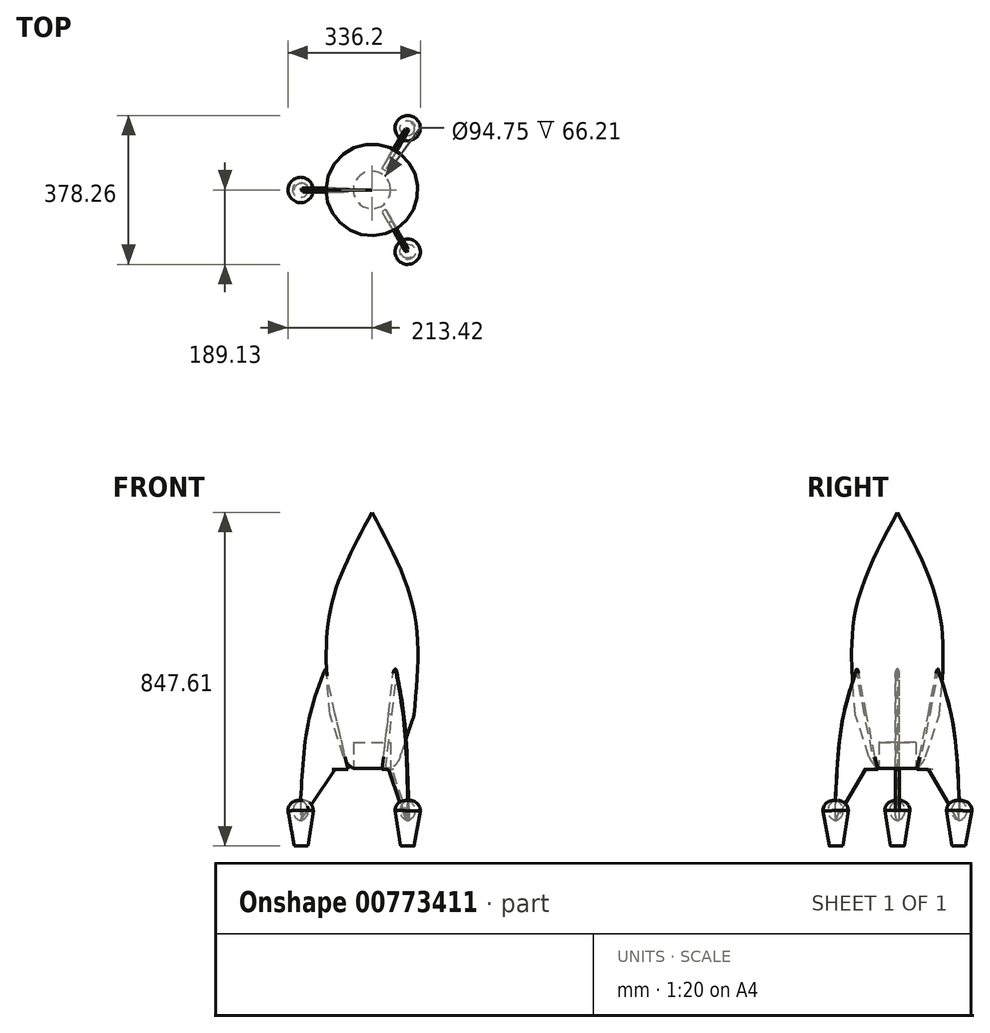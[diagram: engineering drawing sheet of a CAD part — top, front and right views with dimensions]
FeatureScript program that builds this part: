
annotation { "Feature Type Name" : "Feature", "Feature Type Description" : "" }
export const myFeature = defineFeature(function(context is Context, id is Id, definition is map)
    precondition{}
    {
        {
            var Q0;
            Q0=qCreatedBy(makeId("Front.planeOp"),FACE);
            var sketch = newSketch(context, id + "F0", { "sketchPlane" : qUnion([Q0])});
            skLineSegment(sketch, "E0", {"start": v(-61.86, -214.27) * mm, "end": v(-105.8, -81.4) * mm});
            skFitSpline(sketch, "E1", {"points": [v(-106.34, -79.78) * mm, v(-106.34, 186.1) * mm, v(0, 436.45) * mm], "startDerivative": vector(-52.57, 543.97) * mm, "endDerivative": vector(264.66, 488.59) * mm});
            skArc(sketch, "E2.filletArc", {"start": v(-106.5, -78.08) * mm, "mid": v(-106.25, -79.76) * mm, "end": v(-105.8, -81.4) * mm});
            skLineSegment(sketch, "E3", {"start": v(0, -148.06) * mm, "end": v(0, 436.45) * mm});
            skLineSegment(sketch, "E4", {"start": v(-61.86, -214.27) * mm, "end": v(-47.38, -214.27) * mm});
            skLineSegment(sketch, "E5", {"start": v(-47.38, -214.27) * mm, "end": v(-47.38, -148.06) * mm});
            skLineSegment(sketch, "E6", {"start": v(-47.38, -148.06) * mm, "end": v(0, -148.06) * mm});
            skPoint(sketch, "E7.orphan", {"position": v(0, -214.27) * mm});
            skSolve(sketch);
        }
        {
            var Q0;
            Q0=qSketchRegion(id+"F0",true);
            var Q1;
            Q1=sQuery(id+"F0.wireOp",EDGE,"E3");
            revolve(context, id + "F1", {"surfaceOperationType" : NewSurfaceOperationType.NEW, "entities" : qUnion([Q0]), "axis" : qUnion([Q1]), "revolveType" : RevolveType.FULL});
        }
        {
            var Q0;
            Q0=qCreatedBy(makeId("Front.planeOp"),FACE);
            var sketch = newSketch(context, id + "F2", { "sketchPlane" : qUnion([Q0])});
            skFitSpline(sketch, "E8", {"points": [v(-118.68, 38.72) * mm, v(-161.16, -93.41) * mm, v(-181.6, -296.33) * mm], "startDerivative": vector(-106.76, -274.68) * mm, "endDerivative": vector(-21.8, -391.7) * mm});
            skArc(sketch, "E9", {"start": v(-181.6, -296.33) * mm, "mid": v(-206.93, -304.37) * mm, "end": v(-211.8, -330.49) * mm});
            skLineSegment(sketch, "E10", {"start": v(-213.42, -321.5) * mm, "end": v(-197.34, -411.16) * mm});
            skLineSegment(sketch, "E11", {"start": v(-197.34, -411.16) * mm, "end": v(-180.03, -411.16) * mm});
            skLineSegment(sketch, "E12", {"start": v(-180.03, -411.16) * mm, "end": v(-181.6, -296.33) * mm});
            skPoint(sketch, "E13.orphan", {"position": v(-181.6, -346.67) * mm});
            skLineSegment(sketch, "E14", {"start": v(-181.6, -346.67) * mm, "end": v(-93.52, -216.1) * mm});
            skLineSegment(sketch, "E15", {"start": v(-93.52, -216.1) * mm, "end": v(-60.48, -216.1) * mm});
            skLineSegment(sketch, "E16", {"start": v(-60.48, -216.1) * mm, "end": v(-93.52, -76.1) * mm});
            skLineSegment(sketch, "E17", {"start": v(-93.52, -76.1) * mm, "end": v(-118.68, 38.72) * mm});
            skSolve(sketch);
        }
        {
            var Q0;
            {var subQ4=sQuery(id+"F2.wireOp",EDGE,"E8");Q0=makeQuery(id+"F2.imprint","IMPRINT",FACE,{"disambiguationData":[TD([[makeQuery(id+"F2.imprint","IMPRINT",EDGE,{"derivedFrom":subQ4}),1.0]])]});}
            extrude(context, id + "F3", {"entities" : qUnion([Q0]), "endBound" : BoundingType.SYMMETRIC, "depth" : 10.16 * mm, "offsetDistance" : 25.4 * mm});
        }
        {
            var Q0;
            {var subQ0=sQuery(id+"F2.wireOp",EDGE,"E11");Q0=makeQuery(id+"F2.imprint","IMPRINT",FACE,{"disambiguationData":[TD([[makeQuery(id+"F2.imprint","IMPRINT",EDGE,{"derivedFrom":subQ0}),1.0]])]});}
            var Q1;
            Q1=sQuery(id+"F2.wireOp",EDGE,"E12");
            revolve(context, id + "F4", {"surfaceOperationType" : NewSurfaceOperationType.NEW, "entities" : qUnion([Q0]), "axis" : qUnion([Q1]), "revolveType" : RevolveType.FULL});
        }
        {
            var Q0;
            Q0=makeQuery(id+"F3.opExtrude","CAP_EDGE",EDGE,{"disambiguationData":[OSD([sQuery(id+"F2.wireOp",EDGE,"E8")])],"isStart":true});
            var Q1;
            Q1=makeQuery(id+"F3.opExtrude","CAP_EDGE",EDGE,{"disambiguationData":[OSD([sQuery(id+"F2.wireOp",EDGE,"E8")])],"isStart":false});
            var Q2;
            Q2=makeQuery(id+"F3.opExtrude","CAP_EDGE",EDGE,{"disambiguationData":[OSD([sQuery(id+"F2.wireOp",EDGE,"E14")])],"isStart":false});
            fillet(context, id + "F5", {"entities" : qUnion([Q0, Q1, Q2]), "radius" : 6.13 * mm, "tangentPropagation" : true, "allowEdgeOverflow" : false});
        }
        {
            var Q0;
            Q0=qCreatedBy(makeId("Top.planeOp"),FACE);
            var sketch = newSketch(context, id + "F6", { "sketchPlane" : qUnion([Q0])});
            skCircle(sketch, "E18", {"center": v(0, 0) * mm, "radius": 182.26 * mm});
            skSolve(sketch);
        }
        {
            var Q0;
            Q0=makeQuery(id+"F3.opExtrude","SWEPT_BODY",BODY,{"disambiguationData":[OSD([sQuery(id+"F2.wireOp",EDGE,"E8"),sQuery(id+"F2.wireOp",EDGE,"E12"),sQuery(id+"F2.wireOp",EDGE,"E14"),sQuery(id+"F2.wireOp",EDGE,"E15"),sQuery(id+"F2.wireOp",EDGE,"E16"),sQuery(id+"F2.wireOp",EDGE,"E17")])]});
            var Q1;
            Q1=makeQuery(id+"F4.opRevolve","SWEPT_BODY",BODY,{"disambiguationData":[OSD([sQuery(id+"F2.wireOp",EDGE,"E9"),sQuery(id+"F2.wireOp",EDGE,"E10"),sQuery(id+"F2.wireOp",EDGE,"E11"),sQuery(id+"F2.wireOp",EDGE,"E12")])]});
            var Q2;
            Q2=sQuery(id+"F6.wireOp",EDGE,"E18");
            circularPattern(context, id + "F7", {"entities" : qUnion([Q0, Q1]), "axis" : qUnion([Q2]), "angle" : 360 * degree, "instanceCount" : 3, "equalSpace" : true});
        }
        {
            var Q0;
            Q0=makeQuery(id+"F1.opRevolve","SWEPT_FACE",FACE,{"disambiguationData":[OSD([sQuery(id+"F0.wireOp",EDGE,"E0")])]});
            fillet(context, id + "F8", {"entities" : qUnion([Q0]), "radius" : 54.34 * mm, "tangentPropagation" : true, "allowEdgeOverflow" : false});
        }
    });
